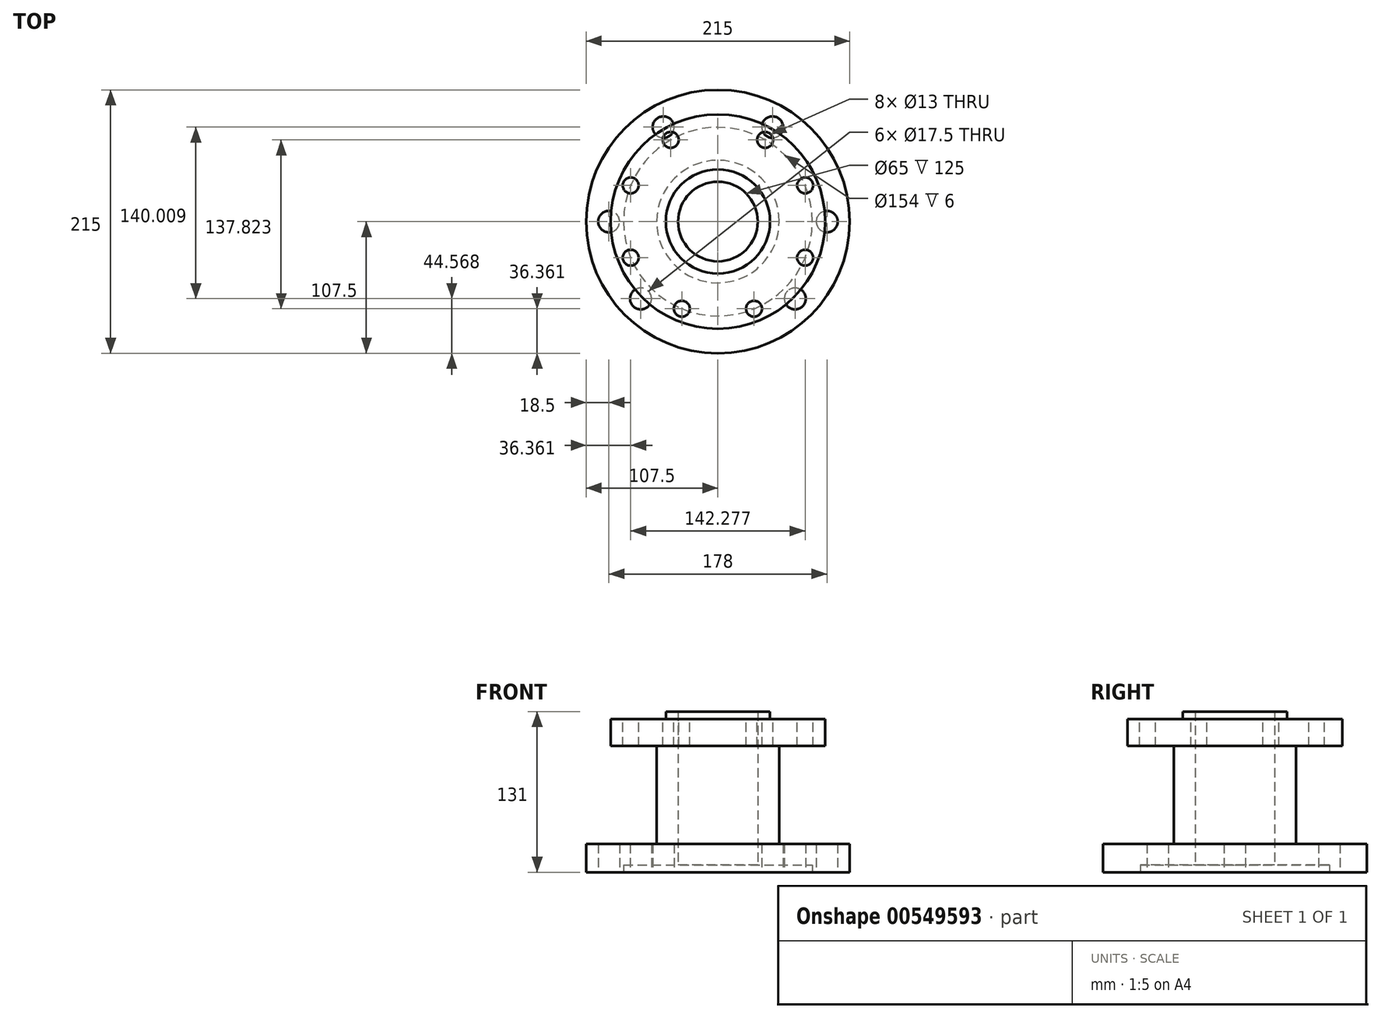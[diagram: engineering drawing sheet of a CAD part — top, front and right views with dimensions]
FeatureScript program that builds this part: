
annotation { "Feature Type Name" : "Feature", "Feature Type Description" : "" }
export const myFeature = defineFeature(function(context is Context, id is Id, definition is map)
    precondition{}
    {
        {
            var Q0;
            Q0=qCreatedBy(makeId("Top.planeOp"),FACE);
            var sketch = newSketch(context, id + "F0", { "sketchPlane" : qUnion([Q0])});
            skCircle(sketch, "E0", {"center": v(0, 0) * mm, "radius": 107.5 * mm});
            skSolve(sketch);
        }
        {
            var Q0;
            Q0=makeQuery(id+"F0.imprint","IMPRINT",FACE,{"disambiguationData":[TD([[makeQuery(id+"F0.imprint","IMPRINT",EDGE,{"derivedFrom":sQuery(id+"F0.wireOp",EDGE,"E0")}),1.0]])]});
            extrude(context, id + "F1", {"entities" : qUnion([Q0]), "depth" : 23 * mm, "offsetDistance" : 25 * mm});
        }
        {
            var Q0;
            Q0=makeQuery(id+"F1.opExtrude","CAP_FACE",FACE,{"disambiguationData":[OSD([sQuery(id+"F0.wireOp",EDGE,"E0")])],"isStart":false});
            var sketch = newSketch(context, id + "F2", { "sketchPlane" : qUnion([Q0])});
            skCircle(sketch, "E1", {"center": v(0, 0) * mm, "radius": 50 * mm});
            skSolve(sketch);
        }
        {
            var Q0;
            Q0=makeQuery(id+"F2.imprint","IMPRINT",FACE,{"disambiguationData":[TD([[makeQuery(id+"F2.imprint","IMPRINT",EDGE,{"derivedFrom":sQuery(id+"F2.wireOp",EDGE,"E1")}),1.0]])]});
            extrude(context, id + "F3", {"entities" : qUnion([Q0]), "operationType" : NewBodyOperationType.ADD, "depth" : 80 * mm, "offsetDistance" : 25 * mm});
        }
        {
            var Q0;
            Q0=makeQuery(id+"F3.opExtrude","CAP_FACE",FACE,{"disambiguationData":[OSD([sQuery(id+"F2.wireOp",EDGE,"E1")])],"isStart":false});
            var sketch = newSketch(context, id + "F4", { "sketchPlane" : qUnion([Q0])});
            skCircle(sketch, "E2", {"center": v(0, 0) * mm, "radius": 87.5 * mm});
            skSolve(sketch);
        }
        {
            var Q0;
            Q0=makeQuery(id+"F4.imprint","IMPRINT",FACE,{"disambiguationData":[TD([[makeQuery(id+"F4.imprint","IMPRINT",EDGE,{"derivedFrom":sQuery(id+"F4.wireOp",EDGE,"E2")}),1.0]])]});
            var Q1;
            Q1=makeQuery(id+"F4.imprint","IMPRINT",FACE,{"disambiguationData":[TD([[makeQuery(id+"F4.imprint","IMPRINT",EDGE,{"derivedFrom":makeQuery(id+"F3.opExtrude","CAP_EDGE",EDGE,{"disambiguationData":[OSD([sQuery(id+"F2.wireOp",EDGE,"E1")])],"isStart":false})}),1.0]])]});
            extrude(context, id + "F5", {"entities" : qUnion([Q0, Q1]), "operationType" : NewBodyOperationType.ADD, "depth" : 22 * mm, "offsetDistance" : 25 * mm});
        }
        {
            var Q0;
            Q0=makeQuery(id+"F5.opExtrude","CAP_FACE",FACE,{"disambiguationData":[OSD([sQuery(id+"F4.wireOp",EDGE,"E2")])],"isStart":false});
            var sketch = newSketch(context, id + "F6", { "sketchPlane" : qUnion([Q0])});
            skCircle(sketch, "E3", {"center": v(0, 0) * mm, "radius": 42.5 * mm});
            skCircle(sketch, "E4", {"center": v(0, 0) * mm, "radius": 32.5 * mm});
            skSolve(sketch);
        }
        {
            var Q0;
            Q0=makeQuery(id+"F6.imprint","IMPRINT",FACE,{"disambiguationData":[TD([[makeQuery(id+"F6.imprint","IMPRINT",EDGE,{"derivedFrom":sQuery(id+"F6.wireOp",EDGE,"E3")}),1.0]])]});
            extrude(context, id + "F7", {"entities" : qUnion([Q0]), "operationType" : NewBodyOperationType.ADD, "depth" : 6 * mm, "offsetDistance" : 25 * mm});
        }
        {
            var Q0;
            Q0=makeQuery(id+"F7.boolean.opBoolean","SPLIT",FACE,{"disambiguationData":[TD([makeQuery(id+"F7.opExtrude","SWEPT_FACE",FACE,{"disambiguationData":[OSD([sQuery(id+"F6.wireOp",EDGE,"E4")])]})])],"derivedFrom":makeQuery(id+"F5.opExtrude","CAP_FACE",FACE,{"disambiguationData":[OSD([sQuery(id+"F4.wireOp",EDGE,"E2")])],"isStart":false})});
            extrude(context, id + "F8", {"entities" : qUnion([Q0]), "operationType" : NewBodyOperationType.REMOVE, "endBound" : BoundingType.THROUGH_ALL, "oppositeDirection" : true, "depth" : 25 * mm, "offsetDistance" : 25 * mm});
        }
        {
            var Q0;
            Q0=makeQuery(id+"F1.opExtrude","CAP_FACE",FACE,{"disambiguationData":[OSD([sQuery(id+"F0.wireOp",EDGE,"E0")])],"isStart":true});
            var sketch = newSketch(context, id + "F9", { "sketchPlane" : qUnion([Q0])});
            skCircle(sketch, "E5", {"center": v(0, 0) * mm, "radius": 77 * mm});
            skSolve(sketch);
        }
        {
            var Q0;
            Q0=makeQuery(id+"F9.imprint","IMPRINT",FACE,{"disambiguationData":[TD([[makeQuery(id+"F9.imprint","IMPRINT",EDGE,{"derivedFrom":sQuery(id+"F9.wireOp",EDGE,"E5")}),1.0]])]});
            extrude(context, id + "F10", {"entities" : qUnion([Q0]), "operationType" : NewBodyOperationType.REMOVE, "oppositeDirection" : true, "depth" : 6 * mm, "offsetDistance" : 25 * mm});
        }
        {
            var Q0;
            {var subQ0=sQuery(id+"F4.wireOp",EDGE,"E2");Q0=makeQuery(id+"F7.boolean.opBoolean","SPLIT",FACE,{"disambiguationData":[TD([makeQuery(id+"F5.opExtrude","SWEPT_FACE",FACE,{"disambiguationData":[OSD([subQ0])]})])],"derivedFrom":makeQuery(id+"F5.opExtrude","CAP_FACE",FACE,{"disambiguationData":[OSD([subQ0])],"isStart":false})});}
            var sketch = newSketch(context, id + "F11", { "sketchPlane" : qUnion([Q0])});
            skCircle(sketch, "E6", {"center": v(0, 0) * mm, "radius": 77 * mm, "construction": true});
            skLineSegment(sketch, "E7", {"start": v(0, 0) * mm, "end": v(0, 139.94) * mm, "construction": true});
            skLineSegment(sketch, "E8", {"start": v(0, 0) * mm, "end": v(0, -134.91) * mm, "construction": true});
            skLineSegment(sketch, "E9", {"start": v(0, 0) * mm, "end": v(136.74, 0) * mm, "construction": true});
            skLineSegment(sketch, "E10", {"start": v(0, 0) * mm, "end": v(-135.78, 0) * mm, "construction": true});
            skLineSegment(sketch, "E11", {"start": v(0, 0) * mm, "end": v(82.95, 143.67) * mm, "construction": true});
            skLineSegment(sketch, "E12", {"start": v(0, 0) * mm, "end": v(144.02, -59.65) * mm, "construction": true});
            skLineSegment(sketch, "E13", {"start": v(0, 0) * mm, "end": v(-73.35, 127.05) * mm, "construction": true});
            skLineSegment(sketch, "E14", {"start": v(0, 0) * mm, "end": v(151.74, 62.85) * mm, "construction": true});
            skLineSegment(sketch, "E15", {"start": v(0, 0) * mm, "end": v(-149.37, 61.87) * mm, "construction": true});
            skLineSegment(sketch, "E16", {"start": v(0, 0) * mm, "end": v(-143.65, -59.5) * mm, "construction": true});
            skLineSegment(sketch, "E17", {"start": v(0, 0) * mm, "end": v(-57.56, -138.95) * mm, "construction": true});
            skLineSegment(sketch, "E18", {"start": v(0, 0) * mm, "end": v(58.71, -141.75) * mm, "construction": true});
            skCircle(sketch, "E19", {"center": v(38.5, 66.68) * mm, "radius": 6.5 * mm});
            skCircle(sketch, "E20", {"center": v(-38.5, 66.68) * mm, "radius": 6.5 * mm});
            skCircle(sketch, "E21", {"center": v(-71.14, 29.47) * mm, "radius": 6.5 * mm});
            skCircle(sketch, "E22", {"center": v(-71.14, -29.47) * mm, "radius": 6.5 * mm});
            skCircle(sketch, "E23", {"center": v(29.47, -71.14) * mm, "radius": 6.5 * mm});
            skCircle(sketch, "E24", {"center": v(-29.47, -71.14) * mm, "radius": 6.5 * mm});
            skCircle(sketch, "E25", {"center": v(71.14, -29.47) * mm, "radius": 6.5 * mm});
            skCircle(sketch, "E26", {"center": v(71.14, 29.47) * mm, "radius": 6.5 * mm});
            skSolve(sketch);
        }
        {
            var Q0;
            Q0=makeQuery(id+"F11.imprint","IMPRINT",FACE,{"disambiguationData":[TD([[makeQuery(id+"F11.imprint","IMPRINT",EDGE,{"derivedFrom":sQuery(id+"F11.wireOp",EDGE,"E20")}),1.0]])]});
            var Q1;
            Q1=makeQuery(id+"F11.imprint","IMPRINT",FACE,{"disambiguationData":[TD([[makeQuery(id+"F11.imprint","IMPRINT",EDGE,{"derivedFrom":sQuery(id+"F11.wireOp",EDGE,"E19")}),1.0]])]});
            var Q2;
            Q2=makeQuery(id+"F11.imprint","IMPRINT",FACE,{"disambiguationData":[TD([[makeQuery(id+"F11.imprint","IMPRINT",EDGE,{"derivedFrom":sQuery(id+"F11.wireOp",EDGE,"E26")}),1.0]])]});
            var Q3;
            Q3=makeQuery(id+"F11.imprint","IMPRINT",FACE,{"disambiguationData":[TD([[makeQuery(id+"F11.imprint","IMPRINT",EDGE,{"derivedFrom":sQuery(id+"F11.wireOp",EDGE,"E25")}),1.0]])]});
            var Q4;
            Q4=makeQuery(id+"F11.imprint","IMPRINT",FACE,{"disambiguationData":[TD([[makeQuery(id+"F11.imprint","IMPRINT",EDGE,{"derivedFrom":sQuery(id+"F11.wireOp",EDGE,"E23")}),1.0]])]});
            var Q5;
            Q5=makeQuery(id+"F11.imprint","IMPRINT",FACE,{"disambiguationData":[TD([[makeQuery(id+"F11.imprint","IMPRINT",EDGE,{"derivedFrom":sQuery(id+"F11.wireOp",EDGE,"E24")}),1.0]])]});
            var Q6;
            Q6=makeQuery(id+"F11.imprint","IMPRINT",FACE,{"disambiguationData":[TD([[makeQuery(id+"F11.imprint","IMPRINT",EDGE,{"derivedFrom":sQuery(id+"F11.wireOp",EDGE,"E22")}),1.0]])]});
            var Q7;
            Q7=makeQuery(id+"F11.imprint","IMPRINT",FACE,{"disambiguationData":[TD([[makeQuery(id+"F11.imprint","IMPRINT",EDGE,{"derivedFrom":sQuery(id+"F11.wireOp",EDGE,"E21")}),1.0]])]});
            extrude(context, id + "F12", {"entities" : qUnion([Q0, Q1, Q2, Q3, Q4, Q5, Q6, Q7]), "operationType" : NewBodyOperationType.REMOVE, "oppositeDirection" : true, "depth" : 25 * mm, "offsetDistance" : 25 * mm});
        }
        {
            var Q0;
            Q0=makeQuery(id+"F1.opExtrude","CAP_FACE",FACE,{"disambiguationData":[OSD([sQuery(id+"F0.wireOp",EDGE,"E0")])],"isStart":true});
            var sketch = newSketch(context, id + "F13", { "sketchPlane" : qUnion([Q0])});
            skCircle(sketch, "E27", {"center": v(0, 0) * mm, "radius": 89 * mm, "construction": true});
            skLineSegment(sketch, "E28", {"start": v(-168.7, 0) * mm, "end": v(171.6, 0) * mm, "construction": true});
            skLineSegment(sketch, "E29", {"start": v(0, 138.82) * mm, "end": v(0, -139.77) * mm, "construction": true});
            skLineSegment(sketch, "E30", {"start": v(0, 0) * mm, "end": v(125.89, 125.89) * mm, "construction": true});
            skLineSegment(sketch, "E31", {"start": v(0, 0) * mm, "end": v(90.74, -157.17) * mm, "construction": true});
            skLineSegment(sketch, "E32", {"start": v(0, 0) * mm, "end": v(-101.75, -176.24) * mm, "construction": true});
            skLineSegment(sketch, "E33", {"start": v(0, 0) * mm, "end": v(-106.05, 106.05) * mm, "construction": true});
            skCircle(sketch, "E34", {"center": v(62.93, 62.93) * mm, "radius": 8.75 * mm});
            skCircle(sketch, "E35", {"center": v(-89, 0) * mm, "radius": 8.75 * mm});
            skCircle(sketch, "E36", {"center": v(-62.93, 62.93) * mm, "radius": 8.75 * mm});
            skCircle(sketch, "E37", {"center": v(-44.5, -77.08) * mm, "radius": 8.75 * mm});
            skCircle(sketch, "E38", {"center": v(44.5, -77.08) * mm, "radius": 8.75 * mm});
            skCircle(sketch, "E39", {"center": v(89, 0) * mm, "radius": 8.75 * mm});
            skSolve(sketch);
        }
        {
            var Q0;
            Q0=makeQuery(id+"F13.imprint","IMPRINT",FACE,{"disambiguationData":[TD([[makeQuery(id+"F13.imprint","IMPRINT",EDGE,{"derivedFrom":sQuery(id+"F13.wireOp",EDGE,"E36")}),1.0]])]});
            var Q1;
            Q1=makeQuery(id+"F13.imprint","IMPRINT",FACE,{"disambiguationData":[TD([[makeQuery(id+"F13.imprint","IMPRINT",EDGE,{"derivedFrom":sQuery(id+"F13.wireOp",EDGE,"E34")}),1.0]])]});
            var Q2;
            Q2=makeQuery(id+"F13.imprint","IMPRINT",FACE,{"disambiguationData":[TD([[makeQuery(id+"F13.imprint","IMPRINT",EDGE,{"derivedFrom":sQuery(id+"F13.wireOp",EDGE,"E39")}),1.0]])]});
            var Q3;
            Q3=makeQuery(id+"F13.imprint","IMPRINT",FACE,{"disambiguationData":[TD([[makeQuery(id+"F13.imprint","IMPRINT",EDGE,{"derivedFrom":sQuery(id+"F13.wireOp",EDGE,"E38")}),1.0]])]});
            var Q4;
            Q4=makeQuery(id+"F13.imprint","IMPRINT",FACE,{"disambiguationData":[TD([[makeQuery(id+"F13.imprint","IMPRINT",EDGE,{"derivedFrom":sQuery(id+"F13.wireOp",EDGE,"E37")}),1.0]])]});
            var Q5;
            Q5=makeQuery(id+"F13.imprint","IMPRINT",FACE,{"disambiguationData":[TD([[makeQuery(id+"F13.imprint","IMPRINT",EDGE,{"derivedFrom":sQuery(id+"F13.wireOp",EDGE,"E35")}),1.0]])]});
            extrude(context, id + "F14", {"entities" : qUnion([Q0, Q1, Q2, Q3, Q4, Q5]), "operationType" : NewBodyOperationType.REMOVE, "oppositeDirection" : true, "depth" : 25 * mm, "offsetDistance" : 25 * mm});
        }
    });
